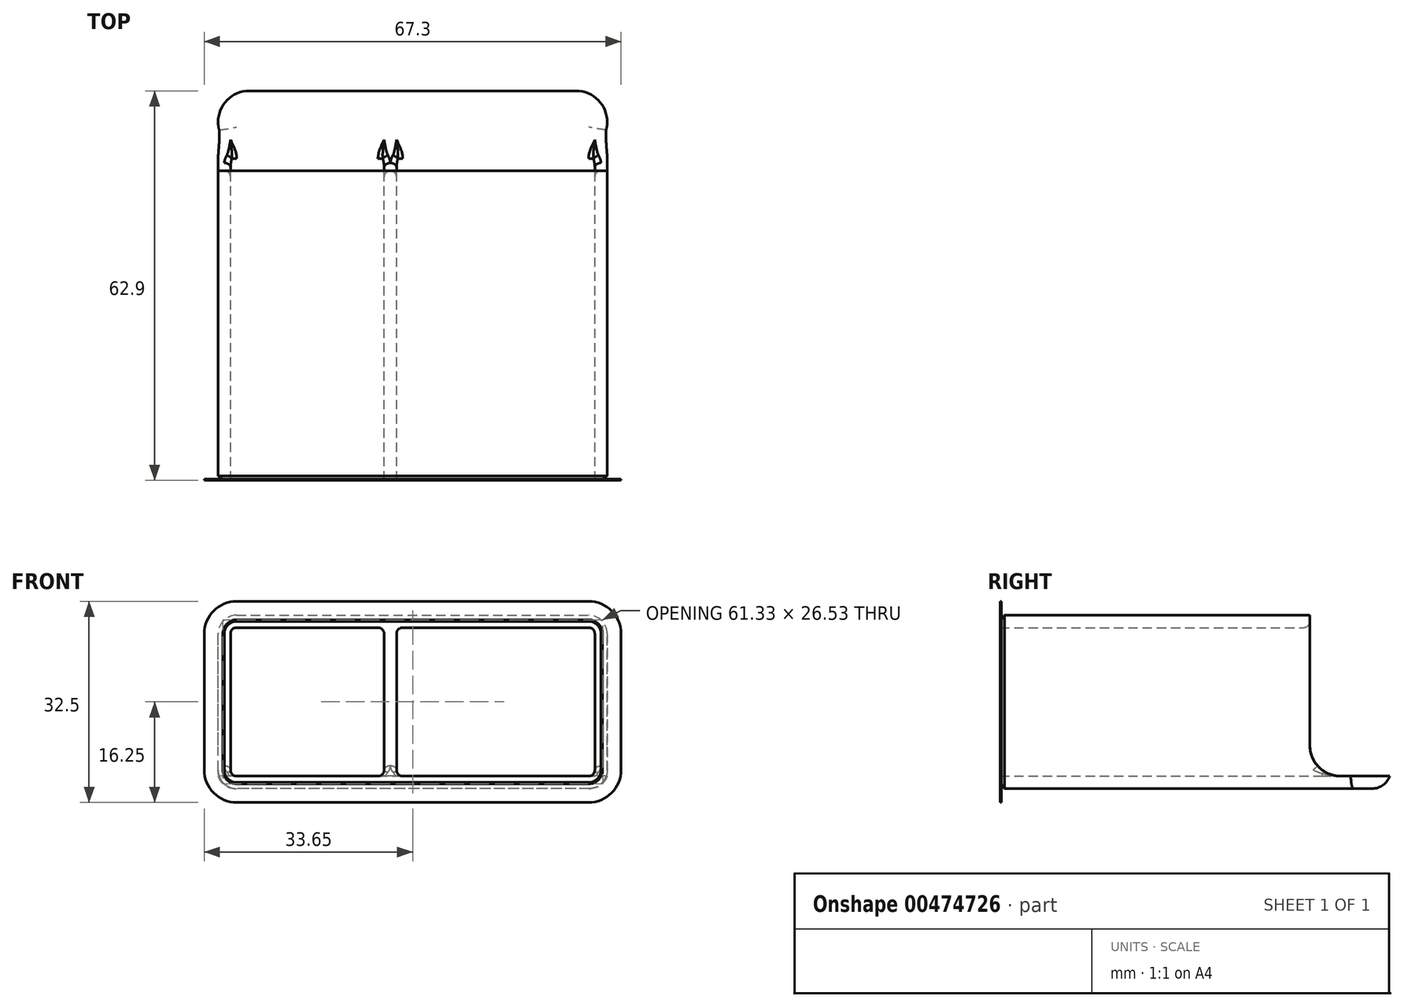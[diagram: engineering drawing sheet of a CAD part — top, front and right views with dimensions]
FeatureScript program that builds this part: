
annotation { "Feature Type Name" : "Feature", "Feature Type Description" : "" }
export const myFeature = defineFeature(function(context is Context, id is Id, definition is map)
    precondition{}
    {
        {
            var Q0;
            Q0=qCreatedBy(makeId("Front.planeOp"),FACE);
            var sketch = newSketch(context, id + "F0", { "sketchPlane" : qUnion([Q0])});
            skLineSegment(sketch, "E0.bottom", {"start": v(0, 0) * mm, "end": v(62.8, 0) * mm});
            skLineSegment(sketch, "E0.top", {"start": v(0, 28) * mm, "end": v(62.8, 28) * mm});
            skLineSegment(sketch, "E0.left", {"start": v(0, 0) * mm, "end": v(0, 28) * mm});
            skLineSegment(sketch, "E0.right", {"start": v(62.8, 0) * mm, "end": v(62.8, 28) * mm});
            skLineSegment(sketch, "E1.bottom", {"start": v(28.8, 26) * mm, "end": v(60.8, 26) * mm});
            skLineSegment(sketch, "E1.top", {"start": v(28.8, 2) * mm, "end": v(60.8, 2) * mm});
            skLineSegment(sketch, "E1.left", {"start": v(28.8, 26) * mm, "end": v(28.8, 2) * mm});
            skLineSegment(sketch, "E1.right", {"start": v(60.8, 26) * mm, "end": v(60.8, 2) * mm});
            skLineSegment(sketch, "E2.bottom", {"start": v(2, 26) * mm, "end": v(26.8, 26) * mm});
            skLineSegment(sketch, "E2.top", {"start": v(2, 2) * mm, "end": v(26.8, 2) * mm});
            skLineSegment(sketch, "E2.left", {"start": v(2, 26) * mm, "end": v(2, 2) * mm});
            skLineSegment(sketch, "E2.right", {"start": v(26.8, 26) * mm, "end": v(26.8, 2) * mm});
            skSolve(sketch);
        }
        {
            var Q0;
            Q0=qSketchRegion(id+"F0",true);
            extrude(context, id + "F1", {"entities" : qUnion([Q0]), "depth" : 62.9 * mm, "offsetDistance" : 25 * mm});
        }
        {
            var Q0;
            Q0=makeQuery(id+"F1.opExtrude","SWEPT_FACE",FACE,{"disambiguationData":[OSD([sQuery(id+"F0.wireOp",EDGE,"E0.top")])]});
            var sketch = newSketch(context, id + "F2", { "sketchPlane" : qUnion([Q0])});
            skLineSegment(sketch, "E3.bottom", {"start": v(0, 0) * mm, "end": v(62.8, 0) * mm});
            skLineSegment(sketch, "E3.top", {"start": v(0, -12.9) * mm, "end": v(62.8, -12.9) * mm});
            skLineSegment(sketch, "E3.left", {"start": v(0, 0) * mm, "end": v(0, -12.9) * mm});
            skLineSegment(sketch, "E3.right", {"start": v(62.8, 0) * mm, "end": v(62.8, -12.9) * mm});
            skSolve(sketch);
        }
        {
            var Q0;
            Q0=qSketchRegion(id+"F2",true);
            var Q1;
            Q1=makeQuery(id+"F1.opExtrude","SWEPT_FACE",FACE,{"disambiguationData":[OSD([sQuery(id+"F0.wireOp",EDGE,"E1.top")])]});
            extrude(context, id + "F3", {"entities" : qUnion([Q0]), "operationType" : NewBodyOperationType.REMOVE, "endBound" : BoundingType.UP_TO_SURFACE, "oppositeDirection" : true, "depth" : 25 * mm, "endBoundEntityFace" : qUnion([Q1]), "offsetDistance" : 25 * mm});
        }
        {
            var Q0;
            Q0=makeQuery(id+"F1.opExtrude","CAP_EDGE",EDGE,{"disambiguationData":[OSD([sQuery(id+"F0.wireOp",EDGE,"E0.right")])],"isStart":true});
            var Q1;
            Q1=makeQuery(id+"F1.opExtrude","CAP_EDGE",EDGE,{"disambiguationData":[OSD([sQuery(id+"F0.wireOp",EDGE,"E0.left")])],"isStart":true});
            fillet(context, id + "F4", {"entities" : qUnion([Q0, Q1]), "radius" : 5 * mm, "tangentPropagation" : true, "allowEdgeOverflow" : false});
        }
        {
            var Q0;
            {var subQ0=sQuery(id+"F2.wireOp",EDGE,"E3.top");Q0=makeQuery(id+"F3.boolean.opBoolean","COPY",EDGE,{"disambiguationData":[TD([makeQuery(id+"F1.opExtrude","SWEPT_FACE",FACE,{"disambiguationData":[OSD([sQuery(id+"F0.wireOp",EDGE,"E0.right")])]})])],"derivedFrom":makeQuery(id+"F3.opExtrude","CAP_EDGE",EDGE,{"disambiguationData":[OSD([subQ0])],"isStart":false})});}
            var Q1;
            {var subQ0=sQuery(id+"F2.wireOp",EDGE,"E3.top");Q1=makeQuery(id+"F3.boolean.opBoolean","COPY",EDGE,{"disambiguationData":[TD([makeQuery(id+"F1.opExtrude","SWEPT_FACE",FACE,{"disambiguationData":[OSD([sQuery(id+"F0.wireOp",EDGE,"E1.left")])]})])],"derivedFrom":makeQuery(id+"F3.opExtrude","CAP_EDGE",EDGE,{"disambiguationData":[OSD([subQ0])],"isStart":false})});}
            var Q2;
            {var subQ0=sQuery(id+"F2.wireOp",EDGE,"E3.top");Q2=makeQuery(id+"F3.boolean.opBoolean","COPY",EDGE,{"disambiguationData":[TD([makeQuery(id+"F1.opExtrude","SWEPT_FACE",FACE,{"disambiguationData":[OSD([sQuery(id+"F0.wireOp",EDGE,"E0.left")])]})])],"derivedFrom":makeQuery(id+"F3.opExtrude","CAP_EDGE",EDGE,{"disambiguationData":[OSD([subQ0])],"isStart":false})});}
            fillet(context, id + "F5", {"entities" : qUnion([Q0, Q1, Q2]), "radius" : 5 * mm, "tangentPropagation" : true, "allowEdgeOverflow" : false});
        }
        {
            var Q0;
            Q0=makeQuery(id+"F1.opExtrude","SWEPT_EDGE",EDGE,{"disambiguationData":[OSD([sQuery(id+"F0.wireOp",EDGE,"E1.top"),sQuery(id+"F0.wireOp",EDGE,"E1.right")])]});
            var Q1;
            Q1=makeQuery(id+"F1.opExtrude","SWEPT_EDGE",EDGE,{"disambiguationData":[OSD([sQuery(id+"F0.wireOp",EDGE,"E1.bottom"),sQuery(id+"F0.wireOp",EDGE,"E1.right")])]});
            var Q2;
            Q2=makeQuery(id+"F1.opExtrude","SWEPT_EDGE",EDGE,{"disambiguationData":[OSD([sQuery(id+"F0.wireOp",EDGE,"E1.bottom"),sQuery(id+"F0.wireOp",EDGE,"E1.left")])]});
            var Q3;
            Q3=makeQuery(id+"F1.opExtrude","SWEPT_EDGE",EDGE,{"disambiguationData":[OSD([sQuery(id+"F0.wireOp",EDGE,"E1.top"),sQuery(id+"F0.wireOp",EDGE,"E1.left")])]});
            var Q4;
            Q4=makeQuery(id+"F1.opExtrude","SWEPT_EDGE",EDGE,{"disambiguationData":[OSD([sQuery(id+"F0.wireOp",EDGE,"E2.top"),sQuery(id+"F0.wireOp",EDGE,"E2.right")])]});
            var Q5;
            Q5=makeQuery(id+"F1.opExtrude","SWEPT_EDGE",EDGE,{"disambiguationData":[OSD([sQuery(id+"F0.wireOp",EDGE,"E2.bottom"),sQuery(id+"F0.wireOp",EDGE,"E2.right")])]});
            var Q6;
            Q6=makeQuery(id+"F1.opExtrude","SWEPT_EDGE",EDGE,{"disambiguationData":[OSD([sQuery(id+"F0.wireOp",EDGE,"E2.bottom"),sQuery(id+"F0.wireOp",EDGE,"E2.left")])]});
            var Q7;
            Q7=makeQuery(id+"F1.opExtrude","SWEPT_EDGE",EDGE,{"disambiguationData":[OSD([sQuery(id+"F0.wireOp",EDGE,"E2.top"),sQuery(id+"F0.wireOp",EDGE,"E2.left")])]});
            fillet(context, id + "F6", {"entities" : qUnion([Q0, Q1, Q2, Q3, Q4, Q5, Q6, Q7]), "radius" : 1 * mm, "tangentPropagation" : true, "allowEdgeOverflow" : false});
        }
        {
            var Q0;
            Q0=makeQuery(id+"F1.opExtrude","SWEPT_EDGE",EDGE,{"disambiguationData":[OSD([sQuery(id+"F0.wireOp",EDGE,"E0.top"),sQuery(id+"F0.wireOp",EDGE,"E0.right")])]});
            var Q1;
            Q1=makeQuery(id+"F1.opExtrude","SWEPT_EDGE",EDGE,{"disambiguationData":[OSD([sQuery(id+"F0.wireOp",EDGE,"E0.top"),sQuery(id+"F0.wireOp",EDGE,"E0.left")])]});
            var Q2;
            Q2=makeQuery(id+"F1.opExtrude","CAP_EDGE",EDGE,{"disambiguationData":[OSD([sQuery(id+"F0.wireOp",EDGE,"E0.bottom")])],"isStart":true});
            fillet(context, id + "F7", {"entities" : qUnion([Q0, Q1, Q2]), "radius" : 3 * mm, "tangentPropagation" : true, "allowEdgeOverflow" : false});
        }
        {
            var Q0;
            Q0=makeQuery(id+"F3.boolean.opBoolean","INTERSECT",EDGE,{"derivedFrom":[makeQuery(id+"F1.opExtrude","SWEPT_FACE",FACE,{"disambiguationData":[OSD([sQuery(id+"F0.wireOp",EDGE,"E2.left")])]}),makeQuery(id+"F3.opExtrude","SWEPT_FACE",FACE,{"disambiguationData":[OSD([sQuery(id+"F2.wireOp",EDGE,"E3.top")])]})]});
            var Q1;
            Q1=makeQuery(id+"F3.boolean.opBoolean","INTERSECT",EDGE,{"derivedFrom":[makeQuery(id+"F1.opExtrude","SWEPT_FACE",FACE,{"disambiguationData":[OSD([sQuery(id+"F0.wireOp",EDGE,"E1.left")])]}),makeQuery(id+"F3.opExtrude","SWEPT_FACE",FACE,{"disambiguationData":[OSD([sQuery(id+"F2.wireOp",EDGE,"E3.top")])]})]});
            fillet(context, id + "F8", {"entities" : qUnion([Q0, Q1]), "radius" : 1 * mm, "tangentPropagation" : true, "allowEdgeOverflow" : false});
        }
        {
            var Q0;
            Q0=makeQuery(id+"F1.opExtrude","CAP_EDGE",EDGE,{"disambiguationData":[OSD([sQuery(id+"F0.wireOp",EDGE,"E0.left")])],"isStart":false});
            chamfer(context, id + "F9", {"entities" : qUnion([Q0]), "chamferType" : ChamferType.TWO_OFFSETS, "width1" : 1 * mm, "oppositeDirection" : false, "width2" : 0.75 * mm, "tangentPropagation" : true});
        }
        {
            var Q0;
            Q0=makeQuery(id+"F1.opExtrude","CAP_FACE",FACE,{"disambiguationData":[OSD([sQuery(id+"F0.wireOp",EDGE,"E0.bottom"),sQuery(id+"F0.wireOp",EDGE,"E0.top"),sQuery(id+"F0.wireOp",EDGE,"E0.left"),sQuery(id+"F0.wireOp",EDGE,"E0.right"),sQuery(id+"F0.wireOp",EDGE,"E1.bottom"),sQuery(id+"F0.wireOp",EDGE,"E1.top"),sQuery(id+"F0.wireOp",EDGE,"E1.left"),sQuery(id+"F0.wireOp",EDGE,"E1.right"),sQuery(id+"F0.wireOp",EDGE,"E2.bottom"),sQuery(id+"F0.wireOp",EDGE,"E2.top"),sQuery(id+"F0.wireOp",EDGE,"E2.left"),sQuery(id+"F0.wireOp",EDGE,"E2.right")])],"isStart":false});
            var sketch = newSketch(context, id + "F10", { "sketchPlane" : qUnion([Q0])});
            skLineSegment(sketch, "E4", {"start": v(0.75, 25) * mm, "end": v(0.75, 3) * mm});
            skLineSegment(sketch, "E5", {"start": v(3, 0.75) * mm, "end": v(59.8, 0.75) * mm});
            skLineSegment(sketch, "E6", {"start": v(3, 27.25) * mm, "end": v(59.8, 27.25) * mm});
            skLineSegment(sketch, "E7", {"start": v(62.05, 25) * mm, "end": v(62.05, 3) * mm});
            skArc(sketch, "E8", {"start": v(3, 27.25) * mm, "mid": v(1.4, 26.6) * mm, "end": v(0.75, 25) * mm});
            skArc(sketch, "E9", {"start": v(62.05, 25) * mm, "mid": v(61.4, 26.6) * mm, "end": v(59.8, 27.25) * mm});
            skArc(sketch, "E10", {"start": v(59.8, 0.75) * mm, "mid": v(61.4, 1.4) * mm, "end": v(62.05, 3) * mm});
            skArc(sketch, "E11", {"start": v(0.75, 3) * mm, "mid": v(1.4, 1.4) * mm, "end": v(3, 0.75) * mm});
            skLineSegment(sketch, "E12", {"start": v(-2.25, 25) * mm, "end": v(-2.25, 3) * mm});
            skLineSegment(sketch, "E13", {"start": v(3, 30.25) * mm, "end": v(59.8, 30.25) * mm});
            skLineSegment(sketch, "E14", {"start": v(3, -2.25) * mm, "end": v(59.8, -2.25) * mm});
            skLineSegment(sketch, "E15", {"start": v(65.05, 25) * mm, "end": v(65.05, 3) * mm});
            skArc(sketch, "E16", {"start": v(3, 30.25) * mm, "mid": v(-0.71, 28.71) * mm, "end": v(-2.25, 25) * mm});
            skArc(sketch, "E17", {"start": v(-2.25, 3) * mm, "mid": v(-0.71, -0.71) * mm, "end": v(3, -2.25) * mm});
            skArc(sketch, "E18", {"start": v(65.05, 25) * mm, "mid": v(63.51, 28.71) * mm, "end": v(59.8, 30.25) * mm});
            skArc(sketch, "E19", {"start": v(59.8, -2.25) * mm, "mid": v(63.51, -0.71) * mm, "end": v(65.05, 3) * mm});
            skSolve(sketch);
        }
        {
            var Q0;
            Q0 = qSketchRegion(id + "F10", true);
            extrude(context, id + "F11", {"entities" : qUnion([Q0]), "operationType" : NewBodyOperationType.ADD, "oppositeDirection" : true, "depth" : 0.2 * mm, "offsetDistance" : 25 * mm});
        }
    });
